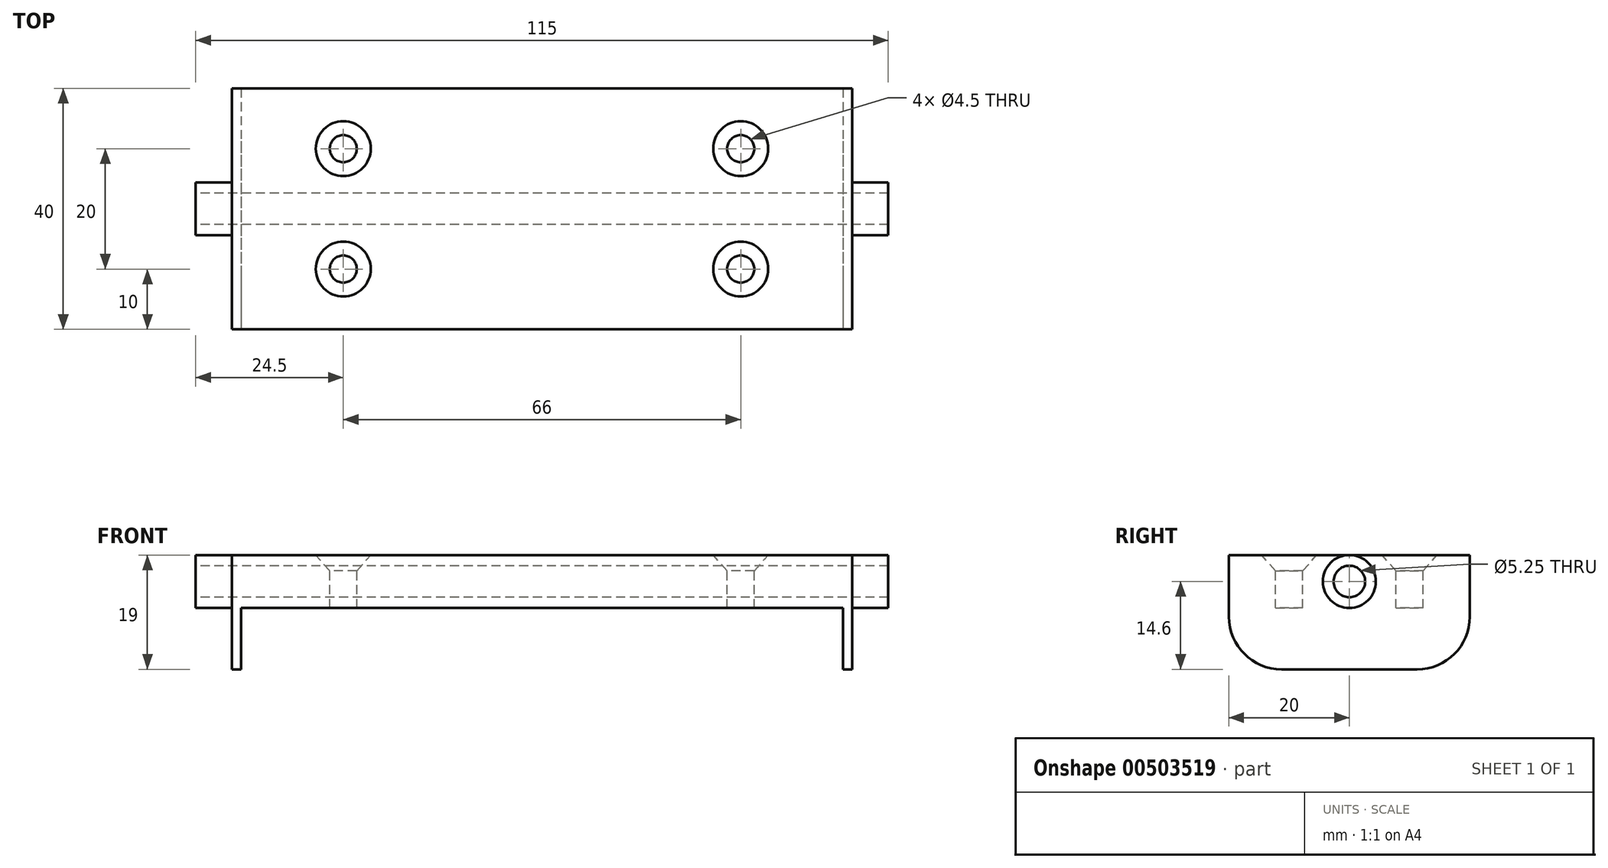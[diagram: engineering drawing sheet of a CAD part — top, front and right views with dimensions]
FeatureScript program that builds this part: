
annotation { "Feature Type Name" : "Feature", "Feature Type Description" : "" }
export const myFeature = defineFeature(function(context is Context, id is Id, definition is map)
    precondition{}
    {
        {
            var Q0;
            Q0=qCreatedBy(makeId("Top.planeOp"),FACE);
            var sketch = newSketch(context, id + "F0", { "sketchPlane" : qUnion([Q0])});
            skLineSegment(sketch, "E0.bottom", {"start": v(50, 20) * mm, "end": v(-50, 20) * mm});
            skLineSegment(sketch, "E0.top", {"start": v(50, -20) * mm, "end": v(-50, -20) * mm});
            skLineSegment(sketch, "E0.left", {"start": v(50, 20) * mm, "end": v(50, -20) * mm});
            skLineSegment(sketch, "E0.right", {"start": v(-50, 20) * mm, "end": v(-50, -20) * mm});
            skPoint(sketch, "E0.middle", {"position": v(0, 0) * mm});
            skLineSegment(sketch, "E1.bottom", {"start": v(-50, 20) * mm, "end": v(-51.5, 20) * mm});
            skLineSegment(sketch, "E1.top", {"start": v(-50, -20) * mm, "end": v(-51.5, -20) * mm});
            skLineSegment(sketch, "E1.right", {"start": v(-51.5, 20) * mm, "end": v(-51.5, -20) * mm});
            skLineSegment(sketch, "E2.bottom", {"start": v(50, 20) * mm, "end": v(51.5, 20) * mm});
            skLineSegment(sketch, "E2.top", {"start": v(50, -20) * mm, "end": v(51.5, -20) * mm});
            skLineSegment(sketch, "E2.right", {"start": v(51.5, 20) * mm, "end": v(51.5, -20) * mm});
            skSolve(sketch);
        }
        {
            var Q0;
            Q0=makeQuery(id+"F0.imprint","IMPRINT",FACE,{"disambiguationData":[TD([[makeQuery(id+"F0.imprint","IMPRINT",EDGE,{"derivedFrom":sQuery(id+"F0.wireOp",EDGE,"E0.bottom")}),1.0]])]});
            var Q1;
            Q1=makeQuery(id+"F0.imprint","IMPRINT",FACE,{"disambiguationData":[TD([[makeQuery(id+"F0.imprint","IMPRINT",EDGE,{"derivedFrom":sQuery(id+"F0.wireOp",EDGE,"E1.bottom")}),1.0]])]});
            var Q2;
            Q2=makeQuery(id+"F0.imprint","IMPRINT",FACE,{"disambiguationData":[TD([[makeQuery(id+"F0.imprint","IMPRINT",EDGE,{"derivedFrom":sQuery(id+"F0.wireOp",EDGE,"E2.bottom")}),-1.0]])]});
            extrude(context, id + "F1", {"entities" : qUnion([Q0, Q1, Q2]), "depth" : 1.5 * mm});
        }
        {
            var Q0;
            Q0=makeQuery(id+"F0.imprint","IMPRINT",FACE,{"disambiguationData":[TD([[makeQuery(id+"F0.imprint","IMPRINT",EDGE,{"derivedFrom":sQuery(id+"F0.wireOp",EDGE,"E1.bottom")}),1.0]])]});
            var Q1;
            Q1=makeQuery(id+"F0.imprint","IMPRINT",FACE,{"disambiguationData":[TD([[makeQuery(id+"F0.imprint","IMPRINT",EDGE,{"derivedFrom":sQuery(id+"F0.wireOp",EDGE,"E2.bottom")}),-1.0]])]});
            extrude(context, id + "F2", {"entities" : qUnion([Q0, Q1]), "operationType" : NewBodyOperationType.ADD, "oppositeDirection" : true, "depth" : (19 - 1.5) * mm});
        }
        {
            var Q0;
            Q0=makeQuery(id+"F0.imprint","IMPRINT",FACE,{"disambiguationData":[TD([[makeQuery(id+"F0.imprint","IMPRINT",EDGE,{"derivedFrom":sQuery(id+"F0.wireOp",EDGE,"E0.bottom")}),1.0]])]});
            extrude(context, id + "F3", {"entities" : qUnion([Q0]), "operationType" : NewBodyOperationType.ADD, "oppositeDirection" : true, "depth" : (8.8 - 1.5) * mm});
        }
        {
            var Q0;
            Q0=qCreatedBy(makeId("Right.planeOp"),FACE);
            var sketch = newSketch(context, id + "F4", { "sketchPlane" : qUnion([Q0])});
            skCircle(sketch, "E3", {"center": v(0, -2.9) * mm, "radius": 4.4 * mm});
            skCircle(sketch, "E4", {"center": v(0, -2.9) * mm, "radius": 2.62 * mm});
            skSolve(sketch);
        }
        {
            var Q0;
            Q0=makeQuery(id+"F4.imprint","IMPRINT",FACE,{"disambiguationData":[TD([[makeQuery(id+"F4.imprint","IMPRINT",EDGE,{"derivedFrom":sQuery(id+"F4.wireOp",EDGE,"E3")}),1.0]])]});
            var Q1;
            Q1=makeQuery(id+"F2.opExtrude","SWEPT_FACE",FACE,{"disambiguationData":[OSD([sQuery(id+"F0.wireOp",EDGE,"E0.left")])]});
            extrude(context, id + "F5", {"entities" : qUnion([Q0]), "operationType" : NewBodyOperationType.ADD, "flatOperationType" : FlatOperationType.REMOVE, "offsetDistance" : 25 * mm, "depth" : 115 * mm, "domain" : OperationDomain.MODEL, "symmetric" : true});
        }
        {
            var Q0;
            Q0=makeQuery(id+"F4.imprint","IMPRINT",FACE,{"disambiguationData":[TD([[makeQuery(id+"F4.imprint","IMPRINT",EDGE,{"derivedFrom":sQuery(id+"F4.wireOp",EDGE,"E4")}),1.0]])]});
            extrude(context, id + "F6", {"entities" : qUnion([Q0]), "operationType" : NewBodyOperationType.REMOVE, "endBound" : BoundingType.THROUGH_ALL, "oppositeDirection" : true, "depth" : 25 * mm, "hasSecondDirection" : true, "secondDirectionBound" : BoundingType.THROUGH_ALL, "secondDirectionOppositeDirection" : false, "secondDirectionDepth" : 25 * mm});
        }
        {
            var Q0;
            Q0=makeQuery(id+"F2.opExtrude","CAP_EDGE",EDGE,{"disambiguationData":[OSD([sQuery(id+"F0.wireOp",EDGE,"E2.top")])],"isStart":false});
            var Q1;
            Q1=makeQuery(id+"F2.opExtrude","CAP_EDGE",EDGE,{"disambiguationData":[OSD([sQuery(id+"F0.wireOp",EDGE,"E2.bottom")])],"isStart":false});
            var Q2;
            Q2=makeQuery(id+"F2.opExtrude","CAP_EDGE",EDGE,{"disambiguationData":[OSD([sQuery(id+"F0.wireOp",EDGE,"E1.top")])],"isStart":false});
            var Q3;
            Q3=makeQuery(id+"F2.opExtrude","CAP_EDGE",EDGE,{"disambiguationData":[OSD([sQuery(id+"F0.wireOp",EDGE,"E1.bottom")])],"isStart":false});
            fillet(context, id + "F7", {"entities" : qUnion([Q0, Q1, Q2, Q3]), "radius" : (19 - 1.5) / 2 * mm, "tangentPropagation" : true, "allowEdgeOverflow" : false});
        }
        {
            var Q0;
            Q0=makeQuery(id+"F1.opExtrude","CAP_FACE",FACE,{"disambiguationData":[OSD([sQuery(id+"F0.wireOp",EDGE,"E0.bottom"),sQuery(id+"F0.wireOp",EDGE,"E0.top"),sQuery(id+"F0.wireOp",EDGE,"E1.bottom"),sQuery(id+"F0.wireOp",EDGE,"E1.top"),sQuery(id+"F0.wireOp",EDGE,"E1.right"),sQuery(id+"F0.wireOp",EDGE,"E2.bottom"),sQuery(id+"F0.wireOp",EDGE,"E2.top"),sQuery(id+"F0.wireOp",EDGE,"E2.right")])],"isStart":false});
            var sketch = newSketch(context, id + "F8", { "sketchPlane" : qUnion([Q0])});
            skLineSegment(sketch, "E5.bottom", {"start": v(33, 10) * mm, "end": v(-33, 10) * mm});
            skLineSegment(sketch, "E5.top", {"start": v(33, -10) * mm, "end": v(-33, -10) * mm});
            skLineSegment(sketch, "E5.left", {"start": v(33, 10) * mm, "end": v(33, -10) * mm});
            skLineSegment(sketch, "E5.right", {"start": v(-33, 10) * mm, "end": v(-33, -10) * mm});
            skPoint(sketch, "E5.middle", {"position": v(0, 0) * mm});
            skSolve(sketch);
        }
        {
            var Q0;
            Q0=sQuery(id+"F8.wireOp",VERTEX,"E5.right.start");
            var Q1;
            Q1=sQuery(id+"F8.wireOp",VERTEX,"E5.right.end");
            var Q2;
            Q2=sQuery(id+"F8.wireOp",VERTEX,"E5.left.end");
            var Q3;
            Q3=sQuery(id+"F8.wireOp",VERTEX,"E5.left.start");
            var Q4;
            Q4=makeQuery(id+"F1.opExtrude","SWEPT_BODY",BODY,{"disambiguationData":[OSD([sQuery(id+"F0.wireOp",EDGE,"E0.bottom"),sQuery(id+"F0.wireOp",EDGE,"E0.top"),sQuery(id+"F0.wireOp",EDGE,"E1.bottom"),sQuery(id+"F0.wireOp",EDGE,"E1.top"),sQuery(id+"F0.wireOp",EDGE,"E1.right"),sQuery(id+"F0.wireOp",EDGE,"E2.bottom"),sQuery(id+"F0.wireOp",EDGE,"E2.top"),sQuery(id+"F0.wireOp",EDGE,"E2.right")])]});
            hole(context, id + "F9", {"style" : HoleStyle.C_SINK, "endStyle" : HoleEndStyle.THROUGH, "standardTappedOrClearance" : lookupTablePath({ "standard" : "ANSI", "fit" : "Normal (ASME)", "size" : "#8", "type" : "Clearance" }), "standardBlindInLast" : lookupTablePath({ "fit" : "Free", "standard" : "ANSI", "size" : "#8", "type" : "Clearance" }), "holeDiameter" : 4.5 * mm, "cSinkDiameter" : 9.12 * mm, "cSinkAngle" : 82 * degree, "isTappedThrough" : true, "tappedDepth" : 46.25 * mm, "tapClearance" : 3, "locations" : qUnion([Q0, Q1, Q2, Q3]), "scope" : qUnion([Q4])});
        }
    });
